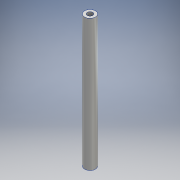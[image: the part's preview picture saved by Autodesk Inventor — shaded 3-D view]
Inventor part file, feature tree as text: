
AUTODESK INVENTOR PART (.ipt)
format: ipt  version: 2016 (Build 200138000, 138)  size: 101,888 bytes
history: native  units: mm
features: sketch x2, extrude x2, hole x2, other x1
ambient origin geometry x8: Origin, YZ Plane, XZ Plane, XY Plane, X Axis, Y Axis, Z Axis, Center Point
bodies: Body1 (feature_tree)
feature tree (7):
  other  "ソリッド1"
  sketch  "スケッチ1"
  extrude  "押し出し1"  Depth=6.0mm
  sketch  "スケッチ2"
  extrude  "押し出し2"  Depth=3.001mm
  hole  "穴1"  [1 undecoded]
  hole  "穴2"  [1 undecoded]
note: 2 required parameter values undecoded (feature->parameter linkage not recoverable at this tier; creation-order binding heuristic only, values carry confidence <= 0.55)
